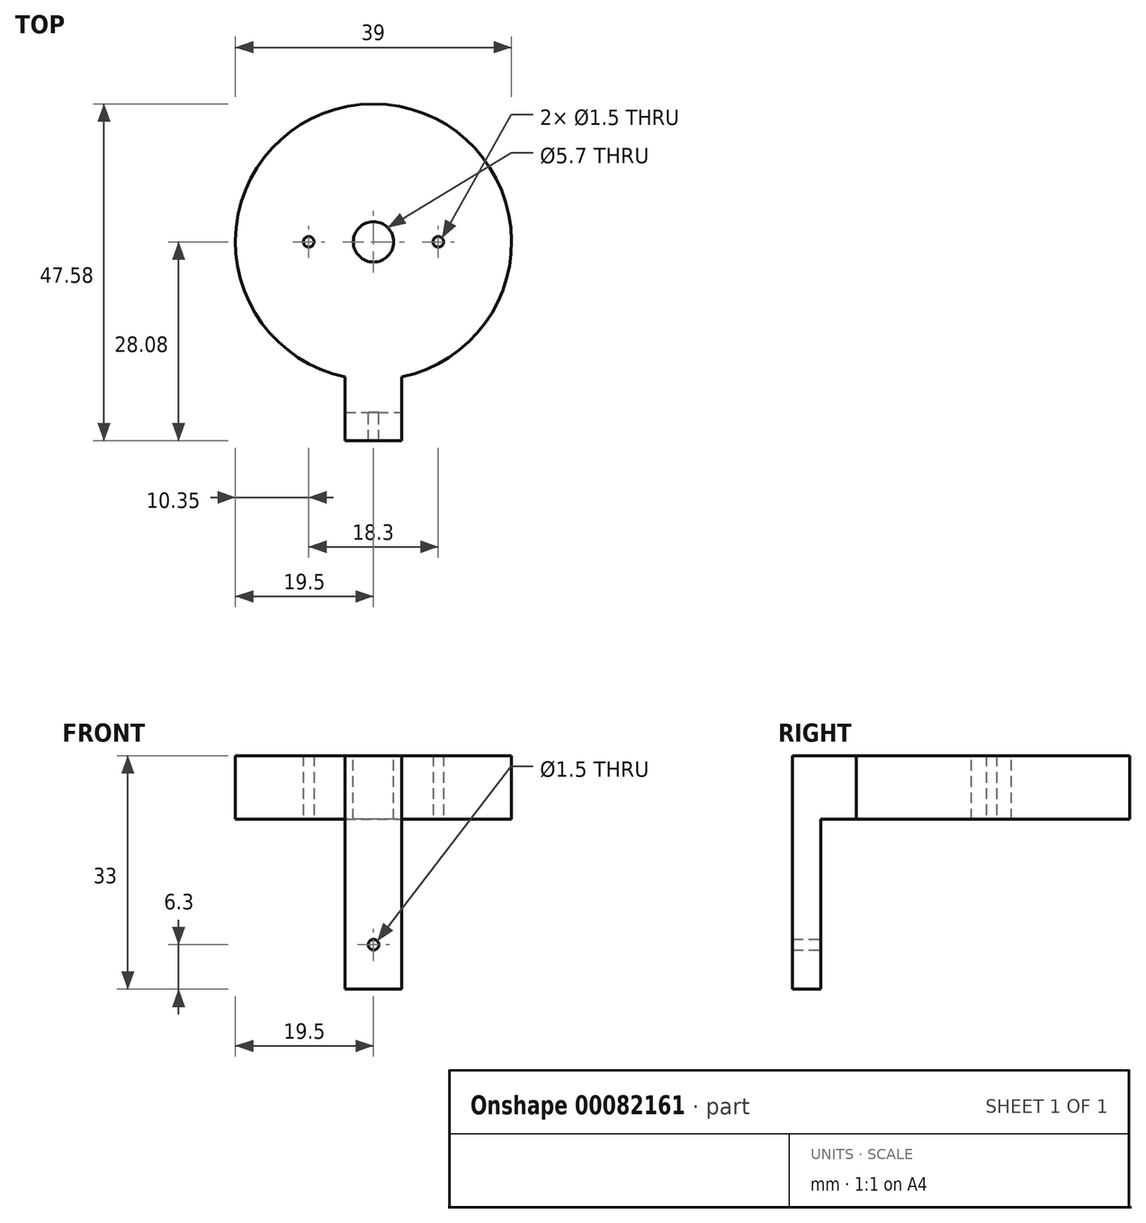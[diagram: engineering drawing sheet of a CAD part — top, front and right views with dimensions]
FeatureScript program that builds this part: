
annotation { "Feature Type Name" : "Feature", "Feature Type Description" : "" }
export const myFeature = defineFeature(function(context is Context, id is Id, definition is map)
    precondition{}
    {
        {
            var Q0;
            Q0=qCreatedBy(makeId("Top.planeOp"),FACE);
            var sketch = newSketch(context, id + "F0", { "sketchPlane" : qUnion([Q0])});
            skCircle(sketch, "E0", {"center": v(0, 0) * mm, "radius": 19.5 * mm});
            skSolve(sketch);
        }
        {
            var Q0;
            Q0 = qSketchRegion(id + "F0", true);
            extrude(context, id + "F1", {"entities" : qUnion([Q0]), "depth" : 9 * mm});
        }
        {
            var Q0;
            Q0=makeQuery(id+"F1.opExtrude","CAP_FACE",FACE,{"disambiguationData":[OSD([sQuery(id+"F0.wireOp",EDGE,"E0")])],"isStart":false});
            var sketch = newSketch(context, id + "F2", { "sketchPlane" : qUnion([Q0])});
            skCircle(sketch, "E1", {"center": v(0, 0) * mm, "radius": 2.85 * mm});
            skSolve(sketch);
        }
        {
            var Q0;
            Q0 = qSketchRegion(id + "F2", true);
            extrude(context, id + "F3", {"entities" : qUnion([Q0]), "operationType" : NewBodyOperationType.REMOVE, "endBound" : BoundingType.THROUGH_ALL, "oppositeDirection" : true, "depth" : 25 * mm});
        }
        {
            var Q0;
            Q0=makeQuery(id+"F1.opExtrude","CAP_FACE",FACE,{"disambiguationData":[OSD([sQuery(id+"F0.wireOp",EDGE,"E0")])],"isStart":true});
            var sketch = newSketch(context, id + "F4", { "sketchPlane" : qUnion([Q0])});
            skLineSegment(sketch, "E2.bottom", {"start": v(-4, 28.08) * mm, "end": v(4, 28.08) * mm});
            skLineSegment(sketch, "E2.top", {"start": v(-4, 19.08) * mm, "end": v(4, 19.08) * mm});
            skLineSegment(sketch, "E2.left", {"start": v(-4, 28.08) * mm, "end": v(-4, 19.08) * mm});
            skLineSegment(sketch, "E2.right", {"start": v(4, 28.08) * mm, "end": v(4, 19.08) * mm});
            skSolve(sketch);
        }
        {
            var Q0;
            Q0 = qSketchRegion(id + "F4", true);
            extrude(context, id + "F5", {"entities" : qUnion([Q0]), "operationType" : NewBodyOperationType.ADD, "oppositeDirection" : true, "depth" : 9 * mm});
        }
        {
            var Q0;
            Q0=makeQuery(id+"F5.boolean.opBoolean","MERGE",FACE,{"derivedFrom":[makeQuery(id+"F1.opExtrude","CAP_FACE",FACE,{"disambiguationData":[OSD([sQuery(id+"F0.wireOp",EDGE,"E0")])],"isStart":true}),makeQuery(id+"F5.opExtrude","CAP_FACE",FACE,{"disambiguationData":[OSD([sQuery(id+"F4.wireOp",EDGE,"E2.bottom"),sQuery(id+"F4.wireOp",EDGE,"E2.top"),sQuery(id+"F4.wireOp",EDGE,"E2.left"),sQuery(id+"F4.wireOp",EDGE,"E2.right")])],"isStart":true})]});
            var sketch = newSketch(context, id + "F6", { "sketchPlane" : qUnion([Q0])});
            skLineSegment(sketch, "E3.bottom", {"start": v(-4, 28.08) * mm, "end": v(4, 28.08) * mm});
            skLineSegment(sketch, "E3.top", {"start": v(-4, 24.08) * mm, "end": v(4, 24.08) * mm});
            skLineSegment(sketch, "E3.left", {"start": v(-4, 28.08) * mm, "end": v(-4, 24.08) * mm});
            skLineSegment(sketch, "E3.right", {"start": v(4, 28.08) * mm, "end": v(4, 24.08) * mm});
            skSolve(sketch);
        }
        {
            var Q0;
            Q0 = qSketchRegion(id + "F6", true);
            extrude(context, id + "F7", {"entities" : qUnion([Q0]), "operationType" : NewBodyOperationType.ADD, "depth" : 24 * mm});
        }
        {
            var Q0;
            Q0=makeQuery(id+"F5.boolean.opBoolean","MERGE",FACE,{"derivedFrom":[makeQuery(id+"F1.opExtrude","CAP_FACE",FACE,{"disambiguationData":[OSD([sQuery(id+"F0.wireOp",EDGE,"E0")])],"isStart":true}),makeQuery(id+"F5.opExtrude","CAP_FACE",FACE,{"disambiguationData":[OSD([sQuery(id+"F4.wireOp",EDGE,"E2.bottom"),sQuery(id+"F4.wireOp",EDGE,"E2.top"),sQuery(id+"F4.wireOp",EDGE,"E2.left"),sQuery(id+"F4.wireOp",EDGE,"E2.right")])],"isStart":true})]});
            var sketch = newSketch(context, id + "F8", { "sketchPlane" : qUnion([Q0])});
            skCircle(sketch, "E4", {"center": v(-9.15, 0) * mm, "radius": 0.75 * mm});
            skLineSegment(sketch, "E5", {"start": v(2.85, 0) * mm, "end": v(9.15, 0) * mm, "construction": true});
            skLineSegment(sketch, "E6", {"start": v(-2.85, 0) * mm, "end": v(-9.15, 0) * mm, "construction": true});
            skCircle(sketch, "E7", {"center": v(9.15, 0) * mm, "radius": 0.75 * mm});
            skSolve(sketch);
        }
        {
            var Q0;
            Q0 = qSketchRegion(id + "F8", true);
            extrude(context, id + "F9", {"entities" : qUnion([Q0]), "operationType" : NewBodyOperationType.REMOVE, "endBound" : BoundingType.THROUGH_ALL, "oppositeDirection" : true, "depth" : 25 * mm});
        }
        {
            var Q0;
            Q0=makeQuery(id+"F7.opExtrude","SWEPT_FACE",FACE,{"disambiguationData":[OSD([sQuery(id+"F6.wireOp",EDGE,"E3.top")])]});
            var sketch = newSketch(context, id + "F10", { "sketchPlane" : qUnion([Q0])});
            skLineSegment(sketch, "E8", {"start": v(0, -24) * mm, "end": v(0, -17.7) * mm, "construction": true});
            skPoint(sketch, "E8.endSnap0", {"position": v(0, -24) * mm});
            skCircle(sketch, "E9", {"center": v(0, -17.7) * mm, "radius": 0.75 * mm});
            skSolve(sketch);
        }
        {
            var Q0;
            Q0 = qSketchRegion(id + "F10", true);
            extrude(context, id + "F11", {"entities" : qUnion([Q0]), "operationType" : NewBodyOperationType.REMOVE, "endBound" : BoundingType.THROUGH_ALL, "oppositeDirection" : true, "depth" : 25 * mm});
        }
    });
